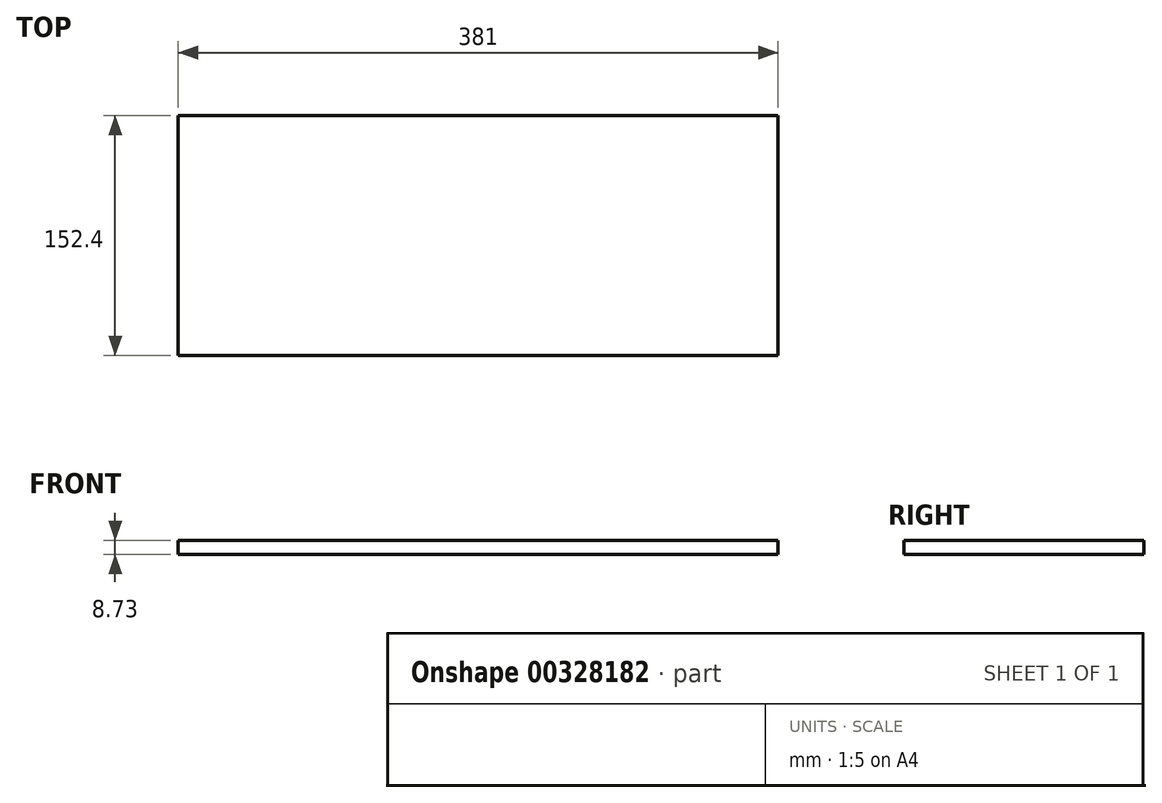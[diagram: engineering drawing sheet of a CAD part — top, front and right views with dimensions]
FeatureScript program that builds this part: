
annotation { "Feature Type Name" : "Feature", "Feature Type Description" : "" }
export const myFeature = defineFeature(function(context is Context, id is Id, definition is map)
    precondition{}
    {
        {
            var Q0;
            Q0=qCreatedBy(makeId("Top.planeOp"),FACE);
            var sketch = newSketch(context, id + "F0", { "sketchPlane" : qUnion([Q0])});
            skLineSegment(sketch, "E0.bottom", {"start": v(-190.5, 76.2) * mm, "end": v(190.5, 76.2) * mm});
            skLineSegment(sketch, "E0.top", {"start": v(-190.5, -76.2) * mm, "end": v(190.5, -76.2) * mm});
            skLineSegment(sketch, "E0.left", {"start": v(-190.5, 76.2) * mm, "end": v(-190.5, -76.2) * mm});
            skLineSegment(sketch, "E0.right", {"start": v(190.5, 76.2) * mm, "end": v(190.5, -76.2) * mm});
            skPoint(sketch, "E0.middle", {"position": v(0, 0) * mm});
            skSolve(sketch);
        }
        {
            var Q0;
            Q0=makeQuery(id+"F0.imprint","IMPRINT",FACE,{"disambiguationData":[TD([[makeQuery(id+"F0.imprint","IMPRINT",EDGE,{"derivedFrom":sQuery(id+"F0.wireOp",EDGE,"E0.bottom")}),-1.0]])]});
            extrude(context, id + "F1", {"entities" : qUnion([Q0]), "depth" : 8.73 * mm});
        }
    });
